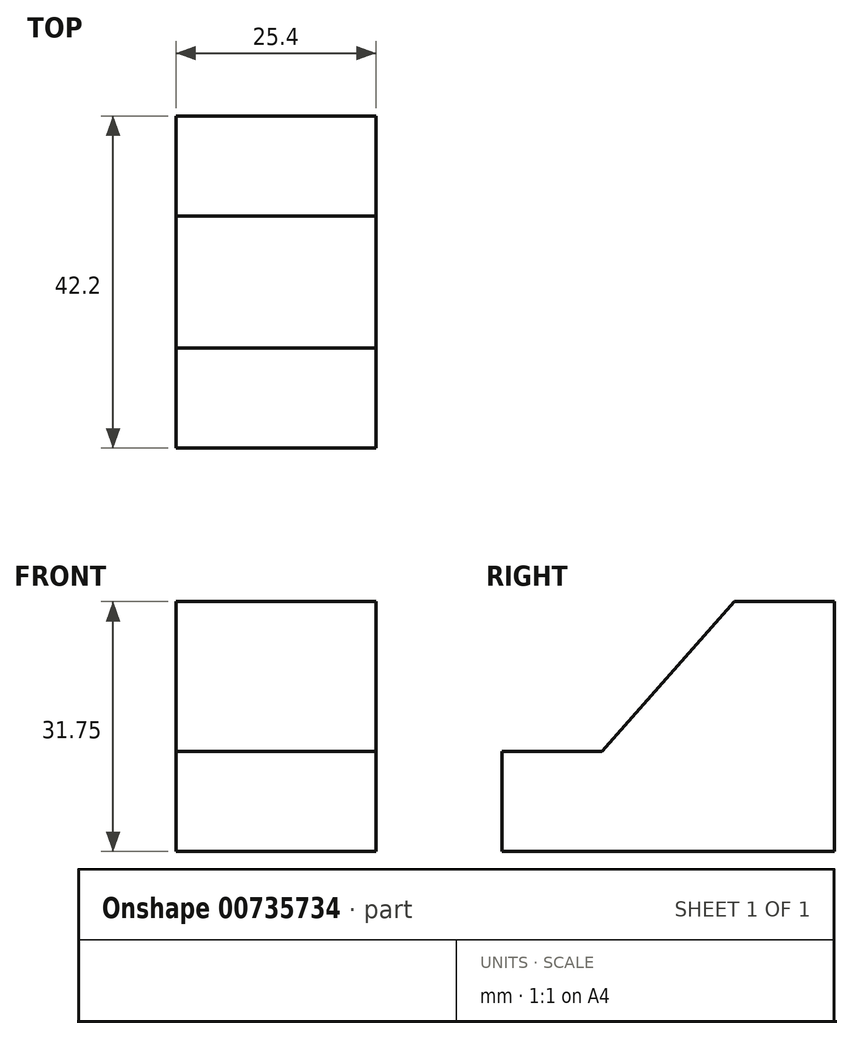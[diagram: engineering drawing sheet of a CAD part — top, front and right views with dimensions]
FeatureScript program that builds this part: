
annotation { "Feature Type Name" : "Feature", "Feature Type Description" : "" }
export const myFeature = defineFeature(function(context is Context, id is Id, definition is map)
    precondition{}
    {
        {
            var Q0;
            Q0=qCreatedBy(makeId("Right.planeOp"),FACE);
            var sketch = newSketch(context, id + "F0", { "sketchPlane" : qUnion([Q0])});
            skLineSegment(sketch, "E0", {"start": v(0, 0) * mm, "end": v(0, 12.7) * mm});
            skLineSegment(sketch, "E1", {"start": v(0, 12.7) * mm, "end": v(12.7, 12.7) * mm});
            skLineSegment(sketch, "E2", {"start": v(12.7, 12.7) * mm, "end": v(29.5, 31.75) * mm});
            skLineSegment(sketch, "E3", {"start": v(29.5, 31.75) * mm, "end": v(42.2, 31.75) * mm});
            skLineSegment(sketch, "E4", {"start": v(42.2, 31.75) * mm, "end": v(42.2, 0) * mm});
            skLineSegment(sketch, "E5", {"start": v(42.2, 0) * mm, "end": v(0, 0) * mm});
            skSolve(sketch);
        }
        {
            var Q0;
            Q0=makeQuery(id+"F0.imprint","IMPRINT",FACE,{"disambiguationData":[TD([[makeQuery(id+"F0.imprint","IMPRINT",EDGE,{"derivedFrom":sQuery(id+"F0.wireOp",EDGE,"E0")}),-1.0]])]});
            extrude(context, id + "F1", {"entities" : qUnion([Q0]), "depth" : 25.4 * mm, "offsetDistance" : 25.4 * mm});
        }
    });
